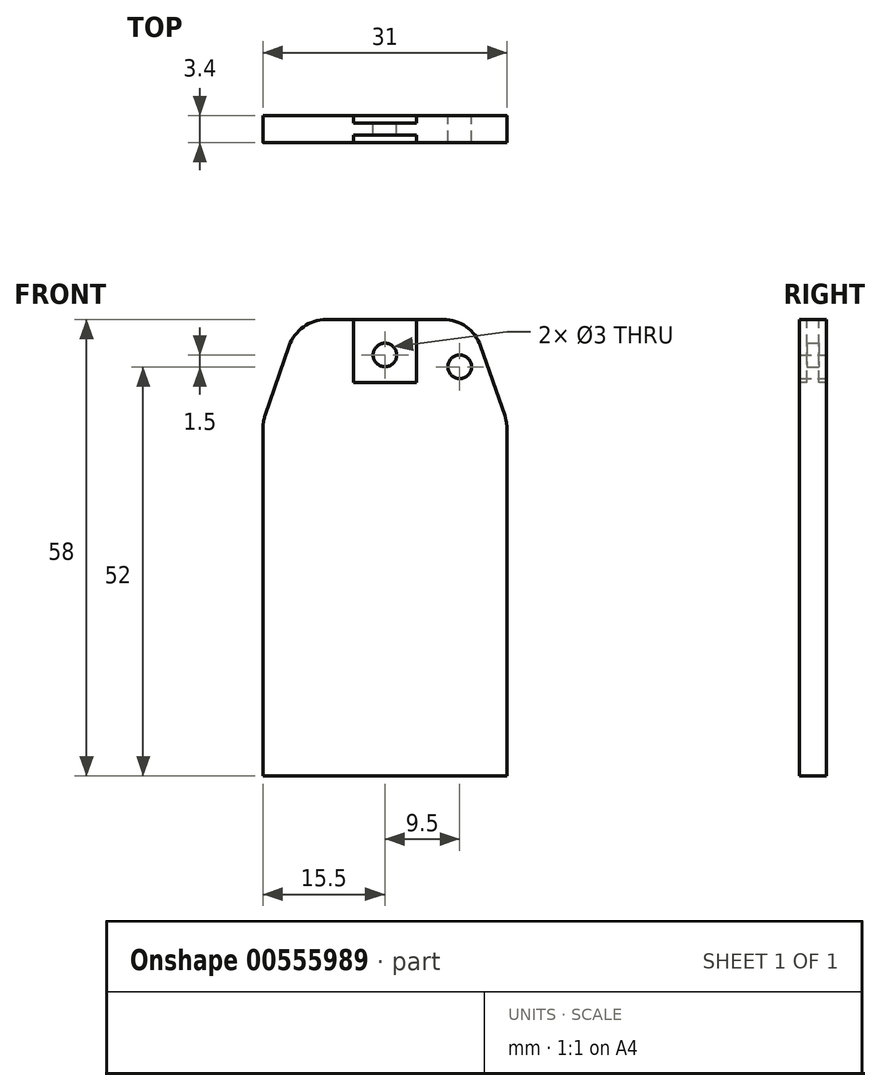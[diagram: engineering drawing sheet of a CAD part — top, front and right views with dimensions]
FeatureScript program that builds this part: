
annotation { "Feature Type Name" : "Feature", "Feature Type Description" : "" }
export const myFeature = defineFeature(function(context is Context, id is Id, definition is map)
    precondition{}
    {
        {
            assignVariable(context, id + "F0", {"name" : "thick", "anyValue" : 3.4});
        }
        {
            var Q0;
            Q0=qCreatedBy(makeId("Front.planeOp"),FACE);
            var sketch = newSketch(context, id + "F1", { "sketchPlane" : qUnion([Q0])});
            skLineSegment(sketch, "E0.bottom", {"start": v(15.5, 22.5) * mm, "end": v(-15.5, 22.5) * mm});
            skLineSegment(sketch, "E0.top", {"start": v(15.5, -22.5) * mm, "end": v(-15.5, -22.5) * mm});
            skLineSegment(sketch, "E0.left", {"start": v(15.5, 22.5) * mm, "end": v(15.5, -22.5) * mm});
            skLineSegment(sketch, "E0.right", {"start": v(-15.5, 22.5) * mm, "end": v(-15.5, -22.5) * mm});
            skPoint(sketch, "E0.middle", {"position": v(0, 0) * mm});
            skLineSegment(sketch, "E1.bottom", {"start": v(11, 35.5) * mm, "end": v(-11, 35.5) * mm});
            skLineSegment(sketch, "E1.top", {"start": v(11, 9.5) * mm, "end": v(-11, 9.5) * mm});
            skLineSegment(sketch, "E1.left", {"start": v(11, 35.5) * mm, "end": v(11, 9.5) * mm});
            skLineSegment(sketch, "E1.right", {"start": v(-11, 35.5) * mm, "end": v(-11, 9.5) * mm});
            skPoint(sketch, "E1.middle", {"position": v(0, 22.5) * mm});
            skLineSegment(sketch, "E2", {"start": v(-11, 35.5) * mm, "end": v(-15.5, 22.5) * mm});
            skLineSegment(sketch, "E3", {"start": v(11, 35.5) * mm, "end": v(15.5, 22.5) * mm});
            skCircle(sketch, "E4", {"center": v(0, 31) * mm, "radius": 1.5 * mm});
            skCircle(sketch, "E5", {"center": v(9.5, 29.5) * mm, "radius": 1.5 * mm});
            skSolve(sketch);
        }
        {
            var Q0;
            Q0 = qSketchRegion(id + "F1", true);
            var Q1;
            {var subQ5=sQuery(id+"F1.wireOp",EDGE,"E1.top");Q1=makeQuery(id+"F1.imprint","IMPRINT",FACE,{"disambiguationData":[TD([[makeQuery(id+"F1.imprint","IMPRINT",EDGE,{"derivedFrom":subQ5}),-1.0]])]});}
            extrude(context, id + "F2", {"entities" : qUnion([Q0, Q1]), "depth" : (getVariable(context, 'thick')) * mm, "offsetDistance" : 25 * mm});
        }
        {
            var Q0;
            Q0=makeQuery(id+"F2.opExtrude","SWEPT_FACE",FACE,{"disambiguationData":[OSD([sQuery(id+"F1.wireOp",EDGE,"E1.bottom")])]});
            var sketch = newSketch(context, id + "F3", { "sketchPlane" : qUnion([Q0])});
            skLineSegment(sketch, "E6.bottom", {"start": v(4, 0) * mm, "end": v(-4, 0) * mm});
            skLineSegment(sketch, "E6.top", {"start": v(4, -3.4) * mm, "end": v(-4, -3.4) * mm});
            skLineSegment(sketch, "E6.left", {"start": v(4, 0) * mm, "end": v(4, -3.4) * mm});
            skLineSegment(sketch, "E6.right", {"start": v(-4, 0) * mm, "end": v(-4, -3.4) * mm});
            skPoint(sketch, "E6.middle.positionSnap0", {"position": v(0, 0) * mm});
            skPoint(sketch, "E6.centerSnap0", {"position": v(0, 0) * mm});
            skPoint(sketch, "E7.middle", {"position": v(4, -3.4) * mm});
            skLineSegment(sketch, "E8", {"start": v(-4, -1.7) * mm, "end": v(4, -1.7) * mm});
            skLineSegment(sketch, "E9.bottom", {"start": v(4, -0.95) * mm, "end": v(-4, -0.95) * mm});
            skLineSegment(sketch, "E9.top", {"start": v(4, -2.45) * mm, "end": v(-4, -2.45) * mm});
            skLineSegment(sketch, "E9.left", {"start": v(4, -0.95) * mm, "end": v(4, -2.45) * mm});
            skLineSegment(sketch, "E9.right", {"start": v(-4, -0.95) * mm, "end": v(-4, -2.45) * mm});
            skPoint(sketch, "E9.middle", {"position": v(0, -1.7) * mm});
            skSolve(sketch);
        }
        {
            var Q0;
            {var subQ0=sQuery(id+"F3.wireOp",EDGE,"E6.bottom");Q0=makeQuery(id+"F3.imprint","IMPRINT",FACE,{"disambiguationData":[TD([[makeQuery(id+"F3.imprint","IMPRINT",EDGE,{"derivedFrom":subQ0}),1.0]])]});}
            extrude(context, id + "F4", {"entities" : qUnion([Q0]), "operationType" : NewBodyOperationType.REMOVE, "oppositeDirection" : true, "depth" : 8 * mm, "offsetDistance" : 25 * mm});
        }
        {
            var Q0;
            {var subQ0=sQuery(id+"F3.wireOp",EDGE,"E6.top");Q0=makeQuery(id+"F3.imprint","IMPRINT",FACE,{"disambiguationData":[TD([[makeQuery(id+"F3.imprint","IMPRINT",EDGE,{"derivedFrom":subQ0}),-1.0]])]});}
            extrude(context, id + "F5", {"entities" : qUnion([Q0]), "operationType" : NewBodyOperationType.REMOVE, "oppositeDirection" : true, "depth" : 8 * mm, "offsetDistance" : 25 * mm});
        }
        {
            var Q0;
            Q0=makeQuery(id+"F2.opExtrude","SWEPT_EDGE",EDGE,{"disambiguationData":[OSD([sQuery(id+"F1.wireOp",EDGE,"E1.bottom"),sQuery(id+"F1.wireOp",EDGE,"E1.right"),sQuery(id+"F1.wireOp",EDGE,"E2")])]});
            fillet(context, id + "F6", {"entities" : qUnion([Q0]), "radius" : 5 * mm, "tangentPropagation" : true, "allowEdgeOverflow" : false});
        }
        {
            var Q0;
            Q0=makeQuery(id+"F2.opExtrude","SWEPT_EDGE",EDGE,{"disambiguationData":[OSD([sQuery(id+"F1.wireOp",EDGE,"E1.bottom"),sQuery(id+"F1.wireOp",EDGE,"E1.left"),sQuery(id+"F1.wireOp",EDGE,"E3")])]});
            fillet(context, id + "F7", {"entities" : qUnion([Q0]), "radius" : 5 * mm, "tangentPropagation" : true, "allowEdgeOverflow" : false});
        }
        {
            var Q0;
            Q0=makeQuery(id+"F2.opExtrude","SWEPT_EDGE",EDGE,{"disambiguationData":[OSD([sQuery(id+"F1.wireOp",EDGE,"E0.bottom"),sQuery(id+"F1.wireOp",EDGE,"E0.left"),sQuery(id+"F1.wireOp",EDGE,"E3")])]});
            fillet(context, id + "F8", {"entities" : qUnion([Q0]), "radius" : 5 * mm, "tangentPropagation" : true, "allowEdgeOverflow" : false});
        }
        {
            var Q0;
            Q0=makeQuery(id+"F2.opExtrude","SWEPT_EDGE",EDGE,{"disambiguationData":[OSD([sQuery(id+"F1.wireOp",EDGE,"E0.bottom"),sQuery(id+"F1.wireOp",EDGE,"E0.right"),sQuery(id+"F1.wireOp",EDGE,"E2")])]});
            fillet(context, id + "F9", {"entities" : qUnion([Q0]), "radius" : 5 * mm, "tangentPropagation" : true, "allowEdgeOverflow" : false});
        }
    });
